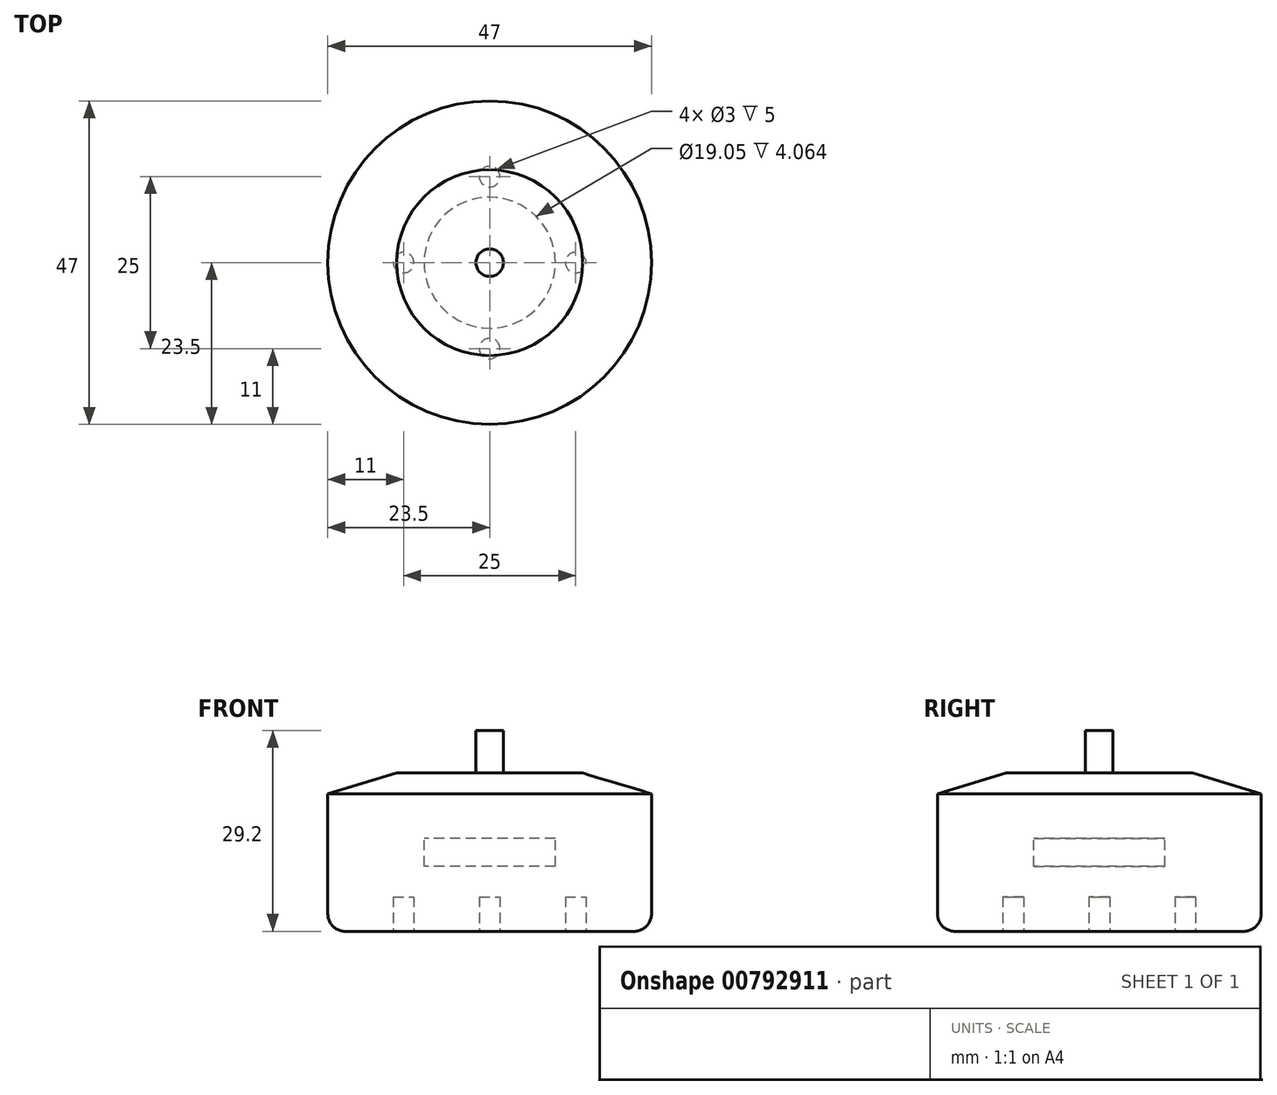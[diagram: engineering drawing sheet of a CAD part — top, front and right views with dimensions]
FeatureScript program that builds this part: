
annotation { "Feature Type Name" : "Feature", "Feature Type Description" : "" }
export const myFeature = defineFeature(function(context is Context, id is Id, definition is map)
    precondition{}
    {
        {
            var Q0;
            Q0=qCreatedBy(makeId("Top.planeOp"),FACE);
            var sketch = newSketch(context, id + "F0", { "sketchPlane" : qUnion([Q0])});
            skCircle(sketch, "E0", {"center": v(0, 0) * mm, "radius": 23.5 * mm});
            skSolve(sketch);
        }
        {
            var Q0;
            Q0 = qSketchRegion(id + "F0", true);
            extrude(context, id + "F1", {"entities" : qUnion([Q0]), "endBound" : BoundingType.SYMMETRIC, "depth" : 23 * mm, "offsetDistance" : 25.4 * mm});
        }
        {
            var Q0;
            Q0=makeQuery(id+"F1.opExtrude","CAP_FACE",FACE,{"disambiguationData":[OSD([sQuery(id+"F0.wireOp",EDGE,"E0")])],"isStart":false});
            var sketch = newSketch(context, id + "F2", { "sketchPlane" : qUnion([Q0])});
            skCircle(sketch, "E1", {"center": v(0, 0) * mm, "radius": 2 * mm});
            skSolve(sketch);
        }
        {
            var Q0;
            Q0 = qSketchRegion(id + "F2", true);
            extrude(context, id + "F3", {"entities" : qUnion([Q0]), "operationType" : NewBodyOperationType.ADD, "depth" : 6.2 * mm, "offsetDistance" : 25.4 * mm});
        }
        {
            var Q0;
            Q0=makeQuery(id+"F1.opExtrude","CAP_FACE",FACE,{"disambiguationData":[OSD([sQuery(id+"F0.wireOp",EDGE,"E0")])],"isStart":true});
            var sketch = newSketch(context, id + "F4", { "sketchPlane" : qUnion([Q0])});
            skCircle(sketch, "E2", {"center": v(0, 0) * mm, "radius": 12.5 * mm, "construction": true});
            skCircle(sketch, "E3", {"center": v(0, 12.5) * mm, "radius": 1.5 * mm});
            skCircle(sketch, "E4.1.0", {"center": v(-12.5, 0) * mm, "radius": 1.5 * mm});
            skCircle(sketch, "E4.2.0", {"center": v(0, -12.5) * mm, "radius": 1.5 * mm});
            skCircle(sketch, "E4.3.0", {"center": v(12.5, 0) * mm, "radius": 1.5 * mm});
            skSolve(sketch);
        }
        {
            var Q0;
            Q0 = qSketchRegion(id + "F4", true);
            extrude(context, id + "F5", {"entities" : qUnion([Q0]), "operationType" : NewBodyOperationType.REMOVE, "oppositeDirection" : true, "depth" : 5 * mm, "offsetDistance" : 25.4 * mm});
        }
        {
            var Q0;
            Q0=makeQuery(id+"F1.opExtrude","CAP_EDGE",EDGE,{"disambiguationData":[OSD([sQuery(id+"F0.wireOp",EDGE,"E0")])],"isStart":false});
            chamfer(context, id + "F6", {"entities" : qUnion([Q0]), "chamferType" : ChamferType.TWO_OFFSETS, "width1" : 10 * mm, "oppositeDirection" : false, "width2" : 3 * mm, "tangentPropagation" : true});
        }
        {
            var Q0;
            Q0=makeQuery(id+"F1.opExtrude","CAP_EDGE",EDGE,{"disambiguationData":[OSD([sQuery(id+"F0.wireOp",EDGE,"E0")])],"isStart":true});
            fillet(context, id + "F7", {"entities" : qUnion([Q0]), "radius" : 2.5 * mm, "tangentPropagation" : true, "allowEdgeOverflow" : false});
        }
        {
            var Q0;
            Q0=qCreatedBy(makeId("Top.planeOp"),FACE);
            var sketch = newSketch(context, id + "F8", { "sketchPlane" : qUnion([Q0])});
            skCircle(sketch, "E5", {"center": v(0, 0) * mm, "radius": 9.53 * mm});
            skSolve(sketch);
        }
        {
            var Q0;
            Q0 = qSketchRegion(id + "F8", true);
            extrude(context, id + "F9", {"entities" : qUnion([Q0]), "operationType" : NewBodyOperationType.REMOVE, "endBound" : BoundingType.SYMMETRIC, "oppositeDirection" : true, "depth" : 4.06 * mm, "offsetDistance" : 25.4 * mm});
        }
    });
